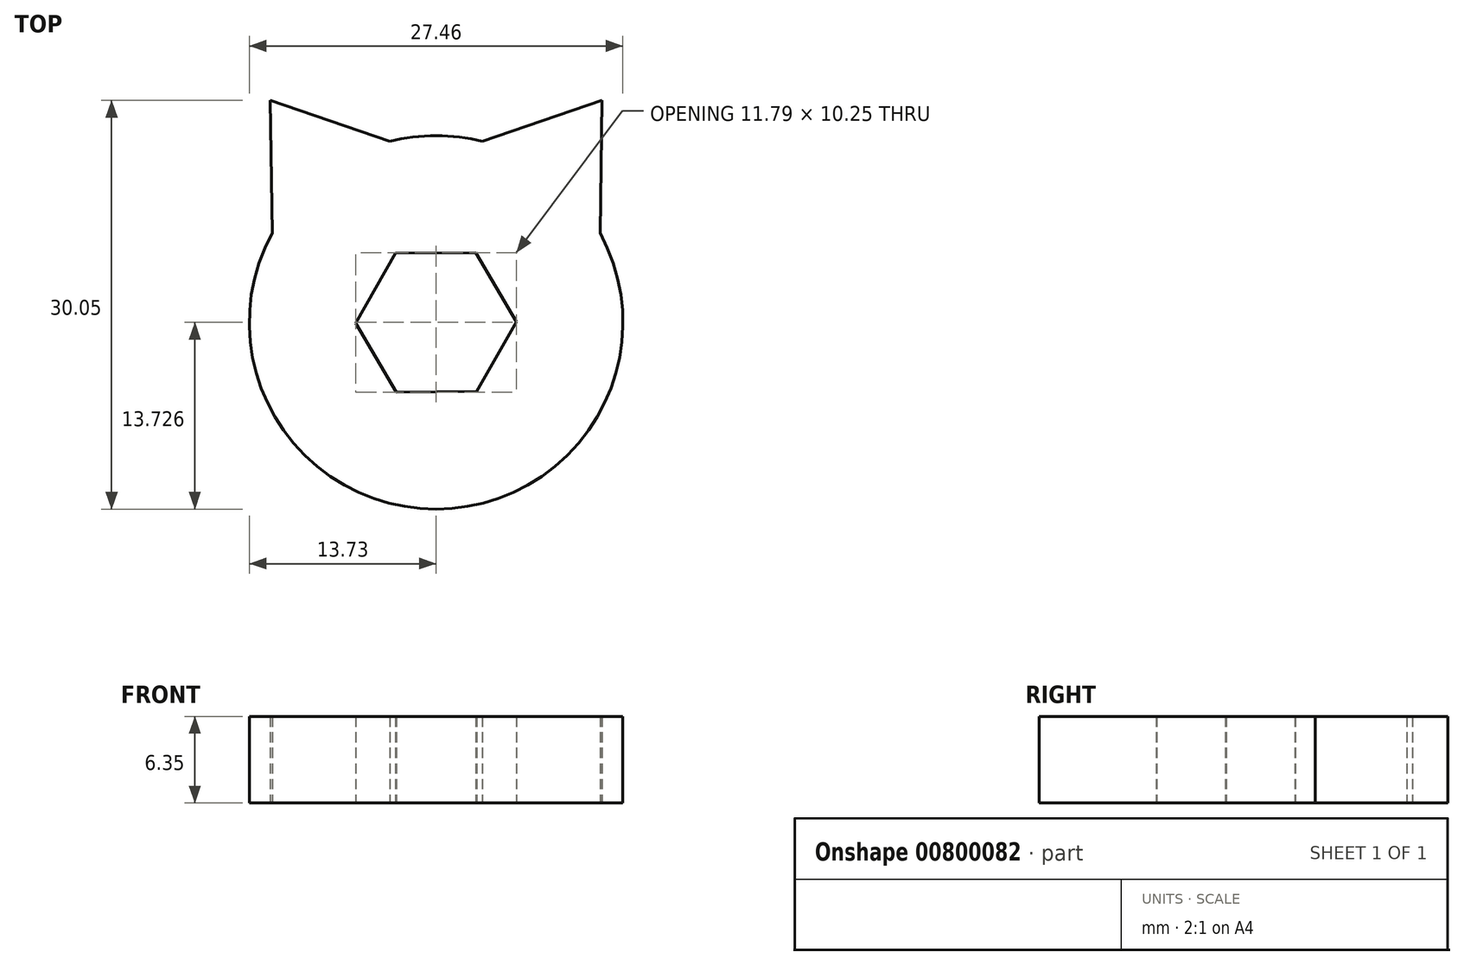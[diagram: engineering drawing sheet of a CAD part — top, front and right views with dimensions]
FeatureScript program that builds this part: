
annotation { "Feature Type Name" : "Feature", "Feature Type Description" : "" }
export const myFeature = defineFeature(function(context is Context, id is Id, definition is map)
    precondition{}
    {
        {
            var Q0;
            Q0=qCreatedBy(makeId("Top.planeOp"),FACE);
            var sketch = newSketch(context, id + "F0", { "sketchPlane" : qUnion([Q0])});
            skCircle(sketch, "E0.cCircle", {"center": v(0, 4.75) * mm, "radius": 5.1 * mm, "construction": true});
            skLineSegment(sketch, "E0.0", {"start": v(2.91, 9.87) * mm, "end": v(5.9, 4.79) * mm});
            skLineSegment(sketch, "E0.1", {"start": v(5.9, 4.79) * mm, "end": v(2.98, -0.34) * mm});
            skLineSegment(sketch, "E0.2", {"start": v(2.98, -0.34) * mm, "end": v(-2.91, -0.38) * mm});
            skLineSegment(sketch, "E0.3", {"start": v(-2.91, -0.38) * mm, "end": v(-5.9, 4.7) * mm});
            skLineSegment(sketch, "E0.4", {"start": v(-5.9, 4.7) * mm, "end": v(-2.98, 9.83) * mm});
            skLineSegment(sketch, "E0.5", {"start": v(-2.98, 9.83) * mm, "end": v(2.91, 9.87) * mm});
            skPoint(sketch, "E0.0.midPoint", {"position": v(4.4, 7.33) * mm});
            skArc(sketch, "E1", {"start": v(-12.05, 11.33) * mm, "mid": v(0, -8.98) * mm, "end": v(12.05, 11.33) * mm});
            skLineSegment(sketch, "E2", {"start": v(-12.19, 21.07) * mm, "end": v(-3.4, 18.05) * mm});
            skLineSegment(sketch, "E3", {"start": v(-12.19, 21.07) * mm, "end": v(-12.05, 11.33) * mm});
            skLineSegment(sketch, "E4", {"start": v(0, 28.16) * mm, "end": v(0, -15.84) * mm, "construction": true});
            skLineSegment(sketch, "E5.MirrorCS", {"start": v(12.19, 21.07) * mm, "end": v(12.05, 11.33) * mm});
            skLineSegment(sketch, "E6.MirrorCS", {"start": v(12.19, 21.07) * mm, "end": v(3.4, 18.05) * mm});
            skArc(sketch, "E7.trimOffspring", {"start": v(3.4, 18.05) * mm, "mid": v(0, 18.47) * mm, "end": v(-3.4, 18.05) * mm});
            skSolve(sketch);
        }
        {
            var Q0;
            Q0=makeQuery(id+"F0.imprint","IMPRINT",FACE,{"disambiguationData":[TD([[makeQuery(id+"F0.imprint","IMPRINT",EDGE,{"derivedFrom":sQuery(id+"F0.wireOp",EDGE,"E0.0")}),1.0]])]});
            extrude(context, id + "F1", {"entities" : qUnion([Q0]), "depth" : 6.35 * mm, "offsetDistance" : 25.4 * mm});
        }
    });
